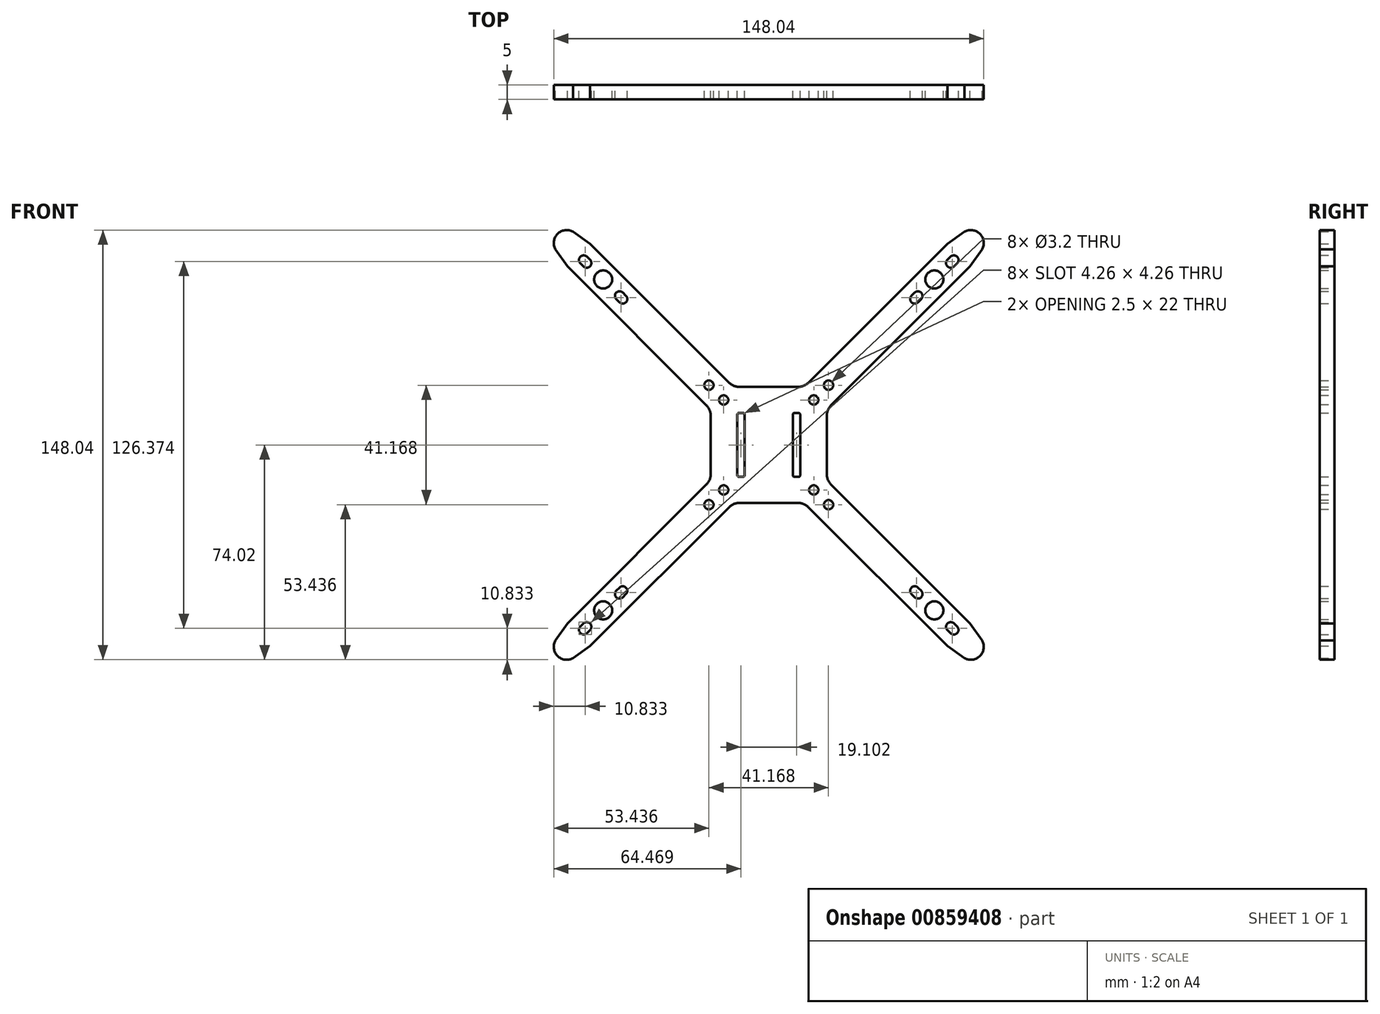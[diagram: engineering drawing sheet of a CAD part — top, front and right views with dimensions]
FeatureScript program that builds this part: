
annotation { "Feature Type Name" : "Feature", "Feature Type Description" : "" }
export const myFeature = defineFeature(function(context is Context, id is Id, definition is map)
    precondition{}
    {
        {
            var Q0;
            Q0=qCreatedBy(makeId("Front.planeOp"),FACE);
            var sketch = newSketch(context, id + "F0", { "sketchPlane" : qUnion([Q0])});
            skLineSegment(sketch, "E0", {"start": v(0, 76.04) * mm, "end": v(0, -62.65) * mm, "construction": true});
            skLineSegment(sketch, "E1", {"start": v(-79.47, 0) * mm, "end": v(81.64, 0) * mm, "construction": true});
            skCircle(sketch, "E2", {"center": v(-57, 57) * mm, "radius": 51.5 * mm, "construction": true});
            skCircle(sketch, "E3.MirrorC", {"center": v(57, 57) * mm, "radius": 51.5 * mm, "construction": true});
            skCircle(sketch, "E4.MirrorC", {"center": v(-57, -57) * mm, "radius": 51.5 * mm, "construction": true});
            skCircle(sketch, "E5.MirrorC", {"center": v(57, -57) * mm, "radius": 51.5 * mm, "construction": true});
            skLineSegment(sketch, "E6", {"start": v(-57, 57) * mm, "end": v(57, 57) * mm, "construction": true});
            skLineSegment(sketch, "E7", {"start": v(-57, 57) * mm, "end": v(-57, -57) * mm, "construction": true});
            skCircle(sketch, "E8", {"center": v(-57, 57) * mm, "radius": 15 * mm, "construction": true});
            skLineSegment(sketch, "E9", {"start": v(-57, 57) * mm, "end": v(-44.49, 69.51) * mm, "construction": true});
            skLineSegment(sketch, "E10.MirrorCS", {"start": v(-57, 57) * mm, "end": v(-69.51, 69.51) * mm, "construction": true});
            skLineSegment(sketch, "E11.MirrorCS", {"start": v(-57, 57) * mm, "end": v(-44.49, 44.49) * mm, "construction": true});
            skLineSegment(sketch, "E12.MirrorCS", {"start": v(-57, 57) * mm, "end": v(-69.51, 44.49) * mm, "construction": true});
            skLineSegment(sketch, "E13.bottom", {"start": v(-10.15, 20) * mm, "end": v(10.15, 20) * mm});
            skLineSegment(sketch, "E13.top", {"start": v(-10.15, -20) * mm, "end": v(10.15, -20) * mm});
            skLineSegment(sketch, "E13.left", {"start": v(-20, 10.15) * mm, "end": v(-20, -10.15) * mm});
            skLineSegment(sketch, "E13.right", {"start": v(20, 10.15) * mm, "end": v(20, -10.15) * mm});
            skLineSegment(sketch, "E14", {"start": v(-57, 57) * mm, "end": v(57, -57) * mm, "construction": true});
            skCircle(sketch, "E15", {"center": v(-15.5, 15.5) * mm, "radius": 1.6 * mm});
            skCircle(sketch, "E16.MirrorC", {"center": v(15.5, 15.5) * mm, "radius": 1.6 * mm});
            skCircle(sketch, "E17.MirrorC", {"center": v(-15.5, -15.5) * mm, "radius": 1.6 * mm});
            skCircle(sketch, "E18.MirrorC", {"center": v(15.5, -15.5) * mm, "radius": 1.6 * mm});
            skArc(sketch, "E19", {"start": v(-62.59, 64.85) * mm, "mid": v(-64.85, 64.85) * mm, "end": v(-64.85, 62.59) * mm});
            skArc(sketch, "E20", {"start": v(-63.79, 61.53) * mm, "mid": v(-61.53, 61.53) * mm, "end": v(-61.53, 63.79) * mm});
            skLineSegment(sketch, "E21", {"start": v(-62.59, 64.85) * mm, "end": v(-61.53, 63.79) * mm});
            skLineSegment(sketch, "E22.MirrorCS", {"start": v(-64.85, 62.59) * mm, "end": v(-63.79, 61.53) * mm});
            skLineSegment(sketch, "E23.MirrorCS", {"start": v(-49.15, 51.41) * mm, "end": v(-50.21, 52.47) * mm});
            skArc(sketch, "E24.MirrorCS", {"start": v(-52.47, 50.21) * mm, "mid": v(-52.47, 52.47) * mm, "end": v(-50.21, 52.47) * mm});
            skLineSegment(sketch, "E25.MirrorCS", {"start": v(-51.41, 49.15) * mm, "end": v(-52.47, 50.21) * mm});
            skArc(sketch, "E26.MirrorCS", {"start": v(-49.15, 51.41) * mm, "mid": v(-49.15, 49.15) * mm, "end": v(-51.41, 49.15) * mm});
            skCircle(sketch, "E27", {"center": v(-57, 57) * mm, "radius": 3.1 * mm});
            skLineSegment(sketch, "E28", {"start": v(-61.5, 69.29) * mm, "end": v(-13.69, 21.46) * mm});
            skLineSegment(sketch, "E29.MirrorCS", {"start": v(-69.29, 61.5) * mm, "end": v(-21.46, 13.69) * mm});
            skArc(sketch, "E30", {"start": v(-67.39, 73.48) * mm, "mid": v(-72.7, 72.7) * mm, "end": v(-73.48, 67.39) * mm});
            skLineSegment(sketch, "E31", {"start": v(-61.5, 69.29) * mm, "end": v(-67.39, 73.48) * mm});
            skLineSegment(sketch, "E32.MirrorCS", {"start": v(-69.29, 61.5) * mm, "end": v(-73.48, 67.39) * mm});
            skLineSegment(sketch, "E33.MirrorCS", {"start": v(64.85, 62.59) * mm, "end": v(63.79, 61.53) * mm});
            skLineSegment(sketch, "E34.MirrorCS", {"start": v(51.41, 49.15) * mm, "end": v(52.47, 50.21) * mm});
            skLineSegment(sketch, "E35.MirrorCS", {"start": v(49.15, 51.41) * mm, "end": v(50.21, 52.47) * mm});
            skLineSegment(sketch, "E36.MirrorCS", {"start": v(62.59, 64.85) * mm, "end": v(61.53, 63.79) * mm});
            skArc(sketch, "E37.MirrorCS", {"start": v(63.79, 61.53) * mm, "mid": v(61.53, 61.53) * mm, "end": v(61.53, 63.79) * mm});
            skArc(sketch, "E38.MirrorCS", {"start": v(52.47, 50.21) * mm, "mid": v(52.47, 52.47) * mm, "end": v(50.21, 52.47) * mm});
            skArc(sketch, "E39.MirrorCS", {"start": v(49.15, 51.41) * mm, "mid": v(49.15, 49.15) * mm, "end": v(51.41, 49.15) * mm});
            skArc(sketch, "E40.MirrorCS", {"start": v(67.39, 73.48) * mm, "mid": v(72.7, 72.7) * mm, "end": v(73.48, 67.39) * mm});
            skCircle(sketch, "E41.MirrorC", {"center": v(57, 57) * mm, "radius": 15 * mm, "construction": true});
            skLineSegment(sketch, "E42.MirrorCS", {"start": v(61.5, 69.29) * mm, "end": v(13.69, 21.46) * mm});
            skLineSegment(sketch, "E43.MirrorCS", {"start": v(69.29, 61.5) * mm, "end": v(21.46, 13.69) * mm});
            skLineSegment(sketch, "E44.MirrorCS", {"start": v(57, 57) * mm, "end": v(44.49, 44.49) * mm, "construction": true});
            skLineSegment(sketch, "E45.MirrorCS", {"start": v(57, 57) * mm, "end": v(69.51, 44.49) * mm, "construction": true});
            skLineSegment(sketch, "E46.MirrorCS", {"start": v(69.29, 61.5) * mm, "end": v(73.48, 67.39) * mm});
            skCircle(sketch, "E47.MirrorC", {"center": v(57, 57) * mm, "radius": 3.1 * mm});
            skLineSegment(sketch, "E48.MirrorCS", {"start": v(61.5, 69.29) * mm, "end": v(67.39, 73.48) * mm});
            skLineSegment(sketch, "E49.MirrorCS", {"start": v(57, 57) * mm, "end": v(69.51, 69.51) * mm, "construction": true});
            skArc(sketch, "E50.MirrorCS", {"start": v(62.59, 64.85) * mm, "mid": v(64.85, 64.85) * mm, "end": v(64.85, 62.59) * mm});
            skLineSegment(sketch, "E51.MirrorCS", {"start": v(57, 57) * mm, "end": v(44.49, 69.51) * mm, "construction": true});
            skLineSegment(sketch, "E52.MirrorCS", {"start": v(-64.85, -62.59) * mm, "end": v(-63.79, -61.53) * mm});
            skLineSegment(sketch, "E53.MirrorCS", {"start": v(-62.59, -64.85) * mm, "end": v(-61.53, -63.79) * mm});
            skLineSegment(sketch, "E54.MirrorCS", {"start": v(-49.15, -51.41) * mm, "end": v(-50.21, -52.47) * mm});
            skLineSegment(sketch, "E55.MirrorCS", {"start": v(-51.41, -49.15) * mm, "end": v(-52.47, -50.21) * mm});
            skArc(sketch, "E56.MirrorCS", {"start": v(-63.79, -61.53) * mm, "mid": v(-61.53, -61.53) * mm, "end": v(-61.53, -63.79) * mm});
            skArc(sketch, "E57.MirrorCS", {"start": v(-62.59, -64.85) * mm, "mid": v(-64.85, -64.85) * mm, "end": v(-64.85, -62.59) * mm});
            skArc(sketch, "E58.MirrorCS", {"start": v(-52.47, -50.21) * mm, "mid": v(-52.47, -52.47) * mm, "end": v(-50.21, -52.47) * mm});
            skLineSegment(sketch, "E59.MirrorCS", {"start": v(-69.29, -61.5) * mm, "end": v(-73.48, -67.39) * mm});
            skLineSegment(sketch, "E60.MirrorCS", {"start": v(-61.5, -69.29) * mm, "end": v(-67.39, -73.48) * mm});
            skCircle(sketch, "E61.MirrorC", {"center": v(-57, -57) * mm, "radius": 3.1 * mm});
            skLineSegment(sketch, "E62.MirrorCS", {"start": v(-69.29, -61.5) * mm, "end": v(-21.46, -13.69) * mm});
            skLineSegment(sketch, "E63.MirrorCS", {"start": v(-57, -57) * mm, "end": v(-69.51, -69.51) * mm, "construction": true});
            skLineSegment(sketch, "E64.MirrorCS", {"start": v(-57, -57) * mm, "end": v(-44.49, -44.49) * mm, "construction": true});
            skLineSegment(sketch, "E65.MirrorCS", {"start": v(-57, -57) * mm, "end": v(-44.49, -69.51) * mm, "construction": true});
            skLineSegment(sketch, "E66.MirrorCS", {"start": v(-61.5, -69.29) * mm, "end": v(-13.69, -21.46) * mm});
            skArc(sketch, "E67.MirrorCS", {"start": v(-49.15, -51.41) * mm, "mid": v(-49.15, -49.15) * mm, "end": v(-51.41, -49.15) * mm});
            skLineSegment(sketch, "E68.MirrorCS", {"start": v(-57, -57) * mm, "end": v(-69.51, -44.49) * mm, "construction": true});
            skCircle(sketch, "E69.MirrorC", {"center": v(-57, -57) * mm, "radius": 15 * mm, "construction": true});
            skArc(sketch, "E70.MirrorCS", {"start": v(-67.39, -73.48) * mm, "mid": v(-72.7, -72.7) * mm, "end": v(-73.48, -67.39) * mm});
            skLineSegment(sketch, "E71.MirrorCS", {"start": v(62.59, -64.85) * mm, "end": v(61.53, -63.79) * mm});
            skLineSegment(sketch, "E72.MirrorCS", {"start": v(51.41, -49.15) * mm, "end": v(52.47, -50.21) * mm});
            skLineSegment(sketch, "E73.MirrorCS", {"start": v(64.85, -62.59) * mm, "end": v(63.79, -61.53) * mm});
            skLineSegment(sketch, "E74.MirrorCS", {"start": v(49.15, -51.41) * mm, "end": v(50.21, -52.47) * mm});
            skArc(sketch, "E75.MirrorCS", {"start": v(67.39, -73.48) * mm, "mid": v(72.7, -72.7) * mm, "end": v(73.48, -67.39) * mm});
            skLineSegment(sketch, "E76.MirrorCS", {"start": v(69.29, -61.5) * mm, "end": v(21.46, -13.69) * mm});
            skArc(sketch, "E77.MirrorCS", {"start": v(52.47, -50.21) * mm, "mid": v(52.47, -52.47) * mm, "end": v(50.21, -52.47) * mm});
            skLineSegment(sketch, "E78.MirrorCS", {"start": v(61.5, -69.29) * mm, "end": v(67.39, -73.48) * mm});
            skLineSegment(sketch, "E79.MirrorCS", {"start": v(57, -57) * mm, "end": v(69.51, -69.51) * mm, "construction": true});
            skLineSegment(sketch, "E80.MirrorCS", {"start": v(69.29, -61.5) * mm, "end": v(73.48, -67.39) * mm});
            skCircle(sketch, "E81.MirrorC", {"center": v(57, -57) * mm, "radius": 15 * mm, "construction": true});
            skLineSegment(sketch, "E82.MirrorCS", {"start": v(57, -57) * mm, "end": v(44.49, -44.49) * mm, "construction": true});
            skLineSegment(sketch, "E83.MirrorCS", {"start": v(57, -57) * mm, "end": v(69.51, -44.49) * mm, "construction": true});
            skLineSegment(sketch, "E84.MirrorCS", {"start": v(57, -57) * mm, "end": v(44.49, -69.51) * mm, "construction": true});
            skArc(sketch, "E85.MirrorCS", {"start": v(62.59, -64.85) * mm, "mid": v(64.85, -64.85) * mm, "end": v(64.85, -62.59) * mm});
            skArc(sketch, "E86.MirrorCS", {"start": v(63.79, -61.53) * mm, "mid": v(61.53, -61.53) * mm, "end": v(61.53, -63.79) * mm});
            skArc(sketch, "E87.MirrorCS", {"start": v(49.15, -51.41) * mm, "mid": v(49.15, -49.15) * mm, "end": v(51.41, -49.15) * mm});
            skLineSegment(sketch, "E88.MirrorCS", {"start": v(61.5, -69.29) * mm, "end": v(13.69, -21.46) * mm});
            skCircle(sketch, "E89.MirrorC", {"center": v(57, -57) * mm, "radius": 3.1 * mm});
            skPoint(sketch, "E90.visualSharp", {"position": v(-12.22, 20) * mm});
            skArc(sketch, "E90.filletArc", {"start": v(-13.69, 21.46) * mm, "mid": v(-12.06, 20.38) * mm, "end": v(-10.15, 20) * mm});
            skPoint(sketch, "E91.visualSharp", {"position": v(12.22, 20) * mm});
            skArc(sketch, "E91.filletArc", {"start": v(10.15, 20) * mm, "mid": v(12.06, 20.38) * mm, "end": v(13.69, 21.46) * mm});
            skPoint(sketch, "E92.visualSharp", {"position": v(20, 12.22) * mm});
            skArc(sketch, "E92.filletArc", {"start": v(21.46, 13.69) * mm, "mid": v(20.38, 12.06) * mm, "end": v(20, 10.15) * mm});
            skPoint(sketch, "E93.visualSharp", {"position": v(20, -12.22) * mm});
            skArc(sketch, "E93.filletArc", {"start": v(20, -10.15) * mm, "mid": v(20.38, -12.06) * mm, "end": v(21.46, -13.69) * mm});
            skPoint(sketch, "E94.visualSharp", {"position": v(12.22, -20) * mm});
            skArc(sketch, "E94.filletArc", {"start": v(13.69, -21.46) * mm, "mid": v(12.06, -20.38) * mm, "end": v(10.15, -20) * mm});
            skPoint(sketch, "E95.visualSharp", {"position": v(-12.22, -20) * mm});
            skArc(sketch, "E95.filletArc", {"start": v(-10.15, -20) * mm, "mid": v(-12.06, -20.38) * mm, "end": v(-13.69, -21.46) * mm});
            skPoint(sketch, "E96.visualSharp", {"position": v(-20, -12.22) * mm});
            skArc(sketch, "E96.filletArc", {"start": v(-21.46, -13.69) * mm, "mid": v(-20.38, -12.06) * mm, "end": v(-20, -10.15) * mm});
            skLineSegment(sketch, "E97.bottom", {"start": v(-10.3, 11) * mm, "end": v(-8.8, 11) * mm});
            skLineSegment(sketch, "E97.top", {"start": v(-10.3, -11) * mm, "end": v(-8.8, -11) * mm});
            skLineSegment(sketch, "E97.left", {"start": v(-10.8, 10.5) * mm, "end": v(-10.8, -10.5) * mm});
            skLineSegment(sketch, "E97.right", {"start": v(-8.3, 10.5) * mm, "end": v(-8.3, -10.5) * mm});
            skPoint(sketch, "E98.visualSharp", {"position": v(-10.8, 11) * mm});
            skArc(sketch, "E98.filletArc", {"start": v(-10.3, 11) * mm, "mid": v(-10.65, 10.85) * mm, "end": v(-10.8, 10.5) * mm});
            skPoint(sketch, "E99.visualSharp", {"position": v(-8.3, 11) * mm});
            skArc(sketch, "E99.filletArc", {"start": v(-8.3, 10.5) * mm, "mid": v(-8.45, 10.85) * mm, "end": v(-8.8, 11) * mm});
            skPoint(sketch, "E100.visualSharp", {"position": v(-8.3, -11) * mm});
            skArc(sketch, "E100.filletArc", {"start": v(-8.8, -11) * mm, "mid": v(-8.45, -10.85) * mm, "end": v(-8.3, -10.5) * mm});
            skPoint(sketch, "E101.visualSharp", {"position": v(-10.8, -11) * mm});
            skArc(sketch, "E101.filletArc", {"start": v(-10.8, -10.5) * mm, "mid": v(-10.65, -10.85) * mm, "end": v(-10.3, -11) * mm});
            skArc(sketch, "E102.MirrorCS", {"start": v(10.8, -10.5) * mm, "mid": v(10.65, -10.85) * mm, "end": v(10.3, -11) * mm});
            skArc(sketch, "E103.MirrorCS", {"start": v(10.3, 11) * mm, "mid": v(10.65, 10.85) * mm, "end": v(10.8, 10.5) * mm});
            skArc(sketch, "E104.MirrorCS", {"start": v(8.8, -11) * mm, "mid": v(8.45, -10.85) * mm, "end": v(8.3, -10.5) * mm});
            skArc(sketch, "E105.MirrorCS", {"start": v(8.3, 10.5) * mm, "mid": v(8.45, 10.85) * mm, "end": v(8.8, 11) * mm});
            skLineSegment(sketch, "E106.MirrorCS", {"start": v(10.3, 11) * mm, "end": v(8.8, 11) * mm});
            skLineSegment(sketch, "E107.MirrorCS", {"start": v(10.3, -11) * mm, "end": v(8.8, -11) * mm});
            skPoint(sketch, "E108.MirrorP", {"position": v(8.3, -11) * mm});
            skLineSegment(sketch, "E109.MirrorCS", {"start": v(10.8, 10.5) * mm, "end": v(10.8, -10.5) * mm});
            skLineSegment(sketch, "E110.MirrorCS", {"start": v(8.3, 10.5) * mm, "end": v(8.3, -10.5) * mm});
            skPoint(sketch, "E111.MirrorP", {"position": v(10.8, -11) * mm});
            skPoint(sketch, "E112.MirrorP", {"position": v(10.8, 11) * mm});
            skPoint(sketch, "E113.MirrorP", {"position": v(8.3, 11) * mm});
            skPoint(sketch, "E114.visualSharp", {"position": v(-20, 12.22) * mm});
            skArc(sketch, "E114.filletArc", {"start": v(-20, 10.15) * mm, "mid": v(-20.38, 12.06) * mm, "end": v(-21.46, 13.69) * mm});
            skCircle(sketch, "E115", {"center": v(-20.58, 20.58) * mm, "radius": 1.6 * mm});
            skCircle(sketch, "E116.MirrorC", {"center": v(20.58, 20.58) * mm, "radius": 1.6 * mm});
            skCircle(sketch, "E117.MirrorC", {"center": v(-20.58, -20.58) * mm, "radius": 1.6 * mm});
            skCircle(sketch, "E118.MirrorC", {"center": v(20.58, -20.58) * mm, "radius": 1.6 * mm});
            skSolve(sketch);
        }
        {
            var Q0;
            Q0 = qSketchRegion(id + "F0", true);
            extrude(context, id + "F1", {"entities" : qUnion([Q0]), "depth" : 5 * mm, "offsetDistance" : 25 * mm});
        }
    });
